# Revit family: QSC CXD4 Amplifiers
name_source: partatom
category: Generic Models
revit_build: Autodesk Revit Architecture 2012 (Build: 20110309_2315(x64)
units: mm (PartAtom-declared; Revit-internal decimal feet)

## types (7) — shared parameters
Default Elevation = 0' - 0"
Height = 0' - 3 1/2"
Manufacturer = QSC Audio Products, LLC
Manufacturer URL = http://www.qscaudio.com
Product Documentation Link = TBD
Product Page URL = TBD
Regulatory Compliance = UL, CE, RoHS/WEEE, FCC Class B
URL = TBD
Voltage AC = 100-240 at 50-60 Hz
Width = 1' - 7"

## per-type parameters (varying)
| type | Depth | Description | Model | Weight Product (kg) | Weight Product (lb) |
| CXD4.2 | 1' - 0" | 2000 Watt Multi-Channel Processing Amplifier | CXD4.2 | 8.4 | 18.5 |
| CXD4.3 @ 100VAC | 1' - 4" | 3000 Watt Multi-Channel Processing Amplifier | CXD4.3 | 9.6 | 21 |
| CXD4.5 @ 100VAC | 1' - 4" | 5000 Watt Multi-Channel Processing Amplifier | CXD4.5 | 10 | 22 |
| CXD4.5 @ 120VAC | 1' - 4" | 5000 Watt Multi-Channel Processing Amplifier | CXD4.5 | 10 | 22 |
| CXD4.5 @ 230VAC | 1' - 4" | 5000 Watt Multi-Channel Processing Amplifier | CXD4.5 | 10 | 22 |
| CXD4.3 @ 120VAC | 1' - 4" | 3000 Watt Multi-Channel Processing Amplifier | CXD4.3 | 9.6 | 21 |
| CXD4.3 @ 230VAC | 1' - 4" | 3000 Watt Multi-Channel Processing Amplifier | CXD4.3 | 9.6 | 21 |

## geometry (parser evidence)
native form markers: Blend x1, Sweep x9
no freeform markers — native parametric forms only
